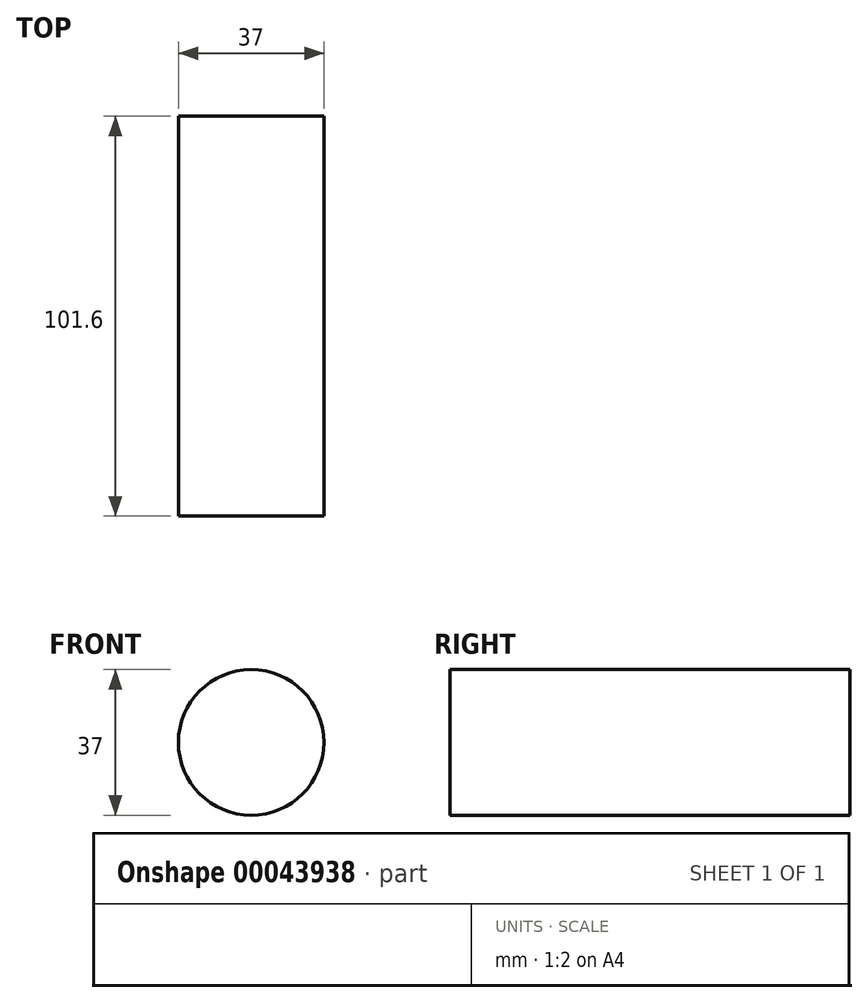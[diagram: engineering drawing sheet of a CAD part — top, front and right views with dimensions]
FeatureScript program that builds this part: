
annotation { "Feature Type Name" : "Feature", "Feature Type Description" : "" }
export const myFeature = defineFeature(function(context is Context, id is Id, definition is map)
    precondition{}
    {
        {
            var Q0;
            Q0=qCreatedBy(makeId("Front.planeOp"),FACE);
            var sketch = newSketch(context, id + "F0", { "sketchPlane" : qUnion([Q0])});
            skCircle(sketch, "E0", {"center": v(0, 0) * mm, "radius": 18.5 * mm});
            skSolve(sketch);
        }
        {
            var Q0;
            Q0=makeQuery(id+"F0.imprint","IMPRINT",FACE,{"disambiguationData":[TD([[makeQuery(id+"F0.imprint","IMPRINT",EDGE,{"derivedFrom":sQuery(id+"F0.wireOp",EDGE,"E0")}),1.0]])]});
            extrude(context, id + "F1", {"entities" : qUnion([Q0]), "endBound" : BoundingType.SYMMETRIC, "depth" : 101.6 * mm});
        }
        {
            var Q0;
            Q0=qCreatedBy(makeId("Top.planeOp"),FACE);
            var sketch = newSketch(context, id + "F2", { "sketchPlane" : qUnion([Q0])});
            skLineSegment(sketch, "E1", {"start": v(0, 51.44) * mm, "end": v(0, -57.73) * mm});
            skSolve(sketch);
        }
        {
            var Q0;
            Q0=qCreatedBy(makeId("Top.planeOp"),FACE);
            var Q1;
            Q1=sQuery(id+"F2.wireOp",EDGE,"E1");
            cPlane(context, id + "F3", {"entities" : qUnion([Q0, Q1]), "cplaneType" : CPlaneType.LINE_ANGLE, "offset" : 152.4 * mm, "angle" : 164 * degree, "width" : 152.4 * mm, "height" : 152.4 * mm});
        }
        {
            var Q0;
            Q0=qCreatedBy(makeId("Front.planeOp"),FACE);
            var sketch = newSketch(context, id + "F4", { "sketchPlane" : qUnion([Q0])});
            skLineSegment(sketch, "E2", {"start": v(0, 0) * mm, "end": v(119.02, 415.07) * mm});
            skSolve(sketch);
        }
        {
            var Q0;
            Q0=qCreatedBy(id+"F3.planeOp",FACE);
            var sketch = newSketch(context, id + "F5", { "sketchPlane" : qUnion([Q0])});
            skCircle(sketch, "E3", {"center": v(0, 0) * mm, "radius": 19.05 * mm});
            skSolve(sketch);
        }
        {
            var Q0;
            Q0=qCreatedBy(makeId("Front.planeOp"),FACE);
            var sketch = newSketch(context, id + "F6", { "sketchPlane" : qUnion([Q0])});
            skLineSegment(sketch, "E4.bottom", {"start": v(0, 0) * mm, "end": v(-444.5, 0) * mm});
            skLineSegment(sketch, "E4.top", {"start": v(0, 622.3) * mm, "end": v(-444.5, 622.3) * mm});
            skLineSegment(sketch, "E4.left", {"start": v(0, 0) * mm, "end": v(0, 622.3) * mm});
            skLineSegment(sketch, "E4.right", {"start": v(-444.5, 0) * mm, "end": v(-444.5, 622.3) * mm});
            skLineSegment(sketch, "E5", {"start": v(-444.5, 622.3) * mm, "end": v(-496.16, 506.28) * mm});
            skLineSegment(sketch, "E6", {"start": v(-488.38, 523.75) * mm, "end": v(-452.22, 604.96) * mm});
            skLineSegment(sketch, "E7", {"start": v(120.8, 414.56) * mm, "end": v(93.48, 316.7) * mm});
            skLineSegment(sketch, "E8", {"start": v(-452.22, 604.96) * mm, "end": v(93.48, 316.7) * mm});
            skLineSegment(sketch, "E9", {"start": v(-488.38, 523.75) * mm, "end": v(0, 0) * mm});
            skSolve(sketch);
        }
        {
            var Q0;
            Q0=qCreatedBy(makeId("Top.planeOp"),FACE);
            var Q1;
            Q1=sQuery(id+"F2.wireOp",EDGE,"E1");
            cPlane(context, id + "F7", {"entities" : qUnion([Q0, Q1]), "cplaneType" : CPlaneType.LINE_ANGLE, "offset" : 152.4 * mm, "angle" : 47 * degree, "width" : 152.4 * mm, "height" : 152.4 * mm});
        }
        {
            var Q0;
            Q0=qCreatedBy(id+"F7.planeOp",FACE);
            var sketch = newSketch(context, id + "F8", { "sketchPlane" : qUnion([Q0])});
            skCircle(sketch, "E10", {"center": v(0, 0) * mm, "radius": 19.05 * mm});
            skSolve(sketch);
        }
        {
            var Q0;
            Q0=qCreatedBy(id+"F7.planeOp",FACE);
            cPlane(context, id + "F9", {"entities" : qUnion([Q0]), "cplaneType" : CPlaneType.OFFSET, "offset" : 716.13 * mm, "oppositeDirection" : true, "width" : 152.4 * mm, "height" : 152.4 * mm});
        }
        {
            var Q0;
            Q0=qCreatedBy(id+"F9.planeOp",FACE);
            var sketch = newSketch(context, id + "F10", { "sketchPlane" : qUnion([Q0])});
            skLineSegment(sketch, "E11", {"start": v(0, 44.85) * mm, "end": v(-178.2, 44.85) * mm});
            skSolve(sketch);
        }
        {
            var Q0;
            Q0=qCreatedBy(id+"F9.planeOp",FACE);
            var Q1;
            Q1=sQuery(id+"F10.wireOp",EDGE,"E11");
            cPlane(context, id + "F11", {"entities" : qUnion([Q0, Q1]), "cplaneType" : CPlaneType.LINE_ANGLE, "offset" : 152.4 * mm, "angle" : 109 * degree, "width" : 152.4 * mm, "height" : 152.4 * mm});
        }
    });
